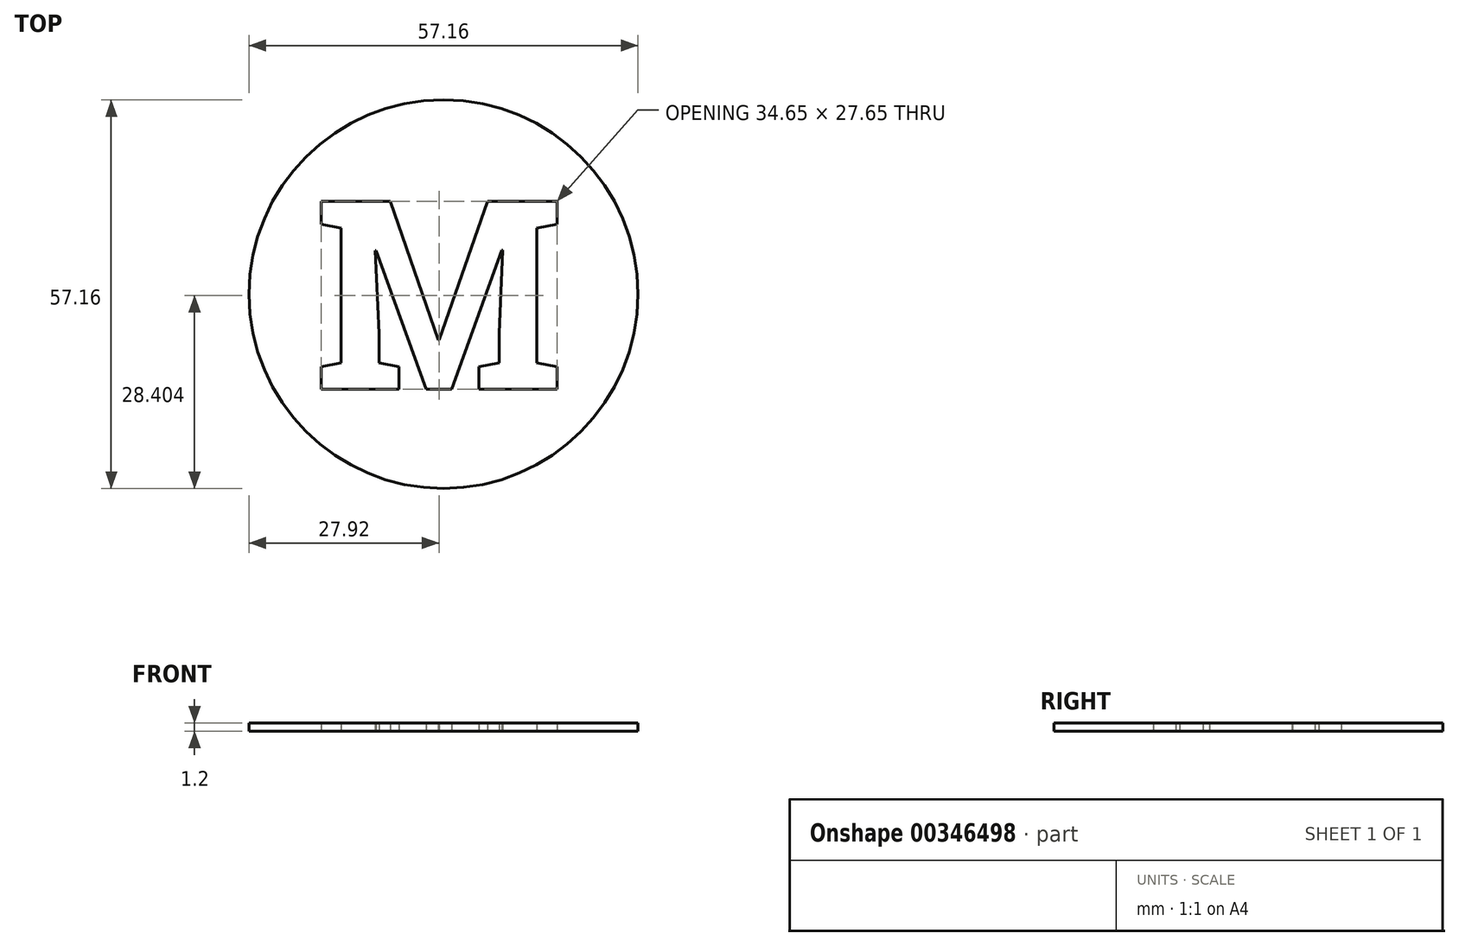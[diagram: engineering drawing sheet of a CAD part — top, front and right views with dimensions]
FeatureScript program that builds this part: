
annotation { "Feature Type Name" : "Feature", "Feature Type Description" : "" }
export const myFeature = defineFeature(function(context is Context, id is Id, definition is map)
    precondition{}
    {
        {
            var Q0;
            Q0=qCreatedBy(makeId("Top.planeOp"),FACE);
            var sketch = newSketch(context, id + "F0", { "sketchPlane" : qUnion([Q0])});
            skCircle(sketch, "E0", {"center": v(0, 0) * mm, "radius": 28.58 * mm});
            skText(sketch, "E1", { "text": "M", "fontName": "RobotoSlab-Bold.ttf"});
            skLineSegment(sketch, "E2", {"start": v(0, 0) * mm, "end": v(19.05, 0) * mm, "construction": true});
            const initialGuessF0  = {"E1": [-0.01905, -0.014, 1, 0, 0.028]};
            skSetInitialGuess(sketch, initialGuessF0);
            skSolve(sketch);
        }
        {
            var Q0;
            Q0 = qSketchRegion(id + "F0", true);
            extrude(context, id + "F1", {"entities" : qUnion([Q0]), "depth" : .2 * 6 * mm});
        }
    });
